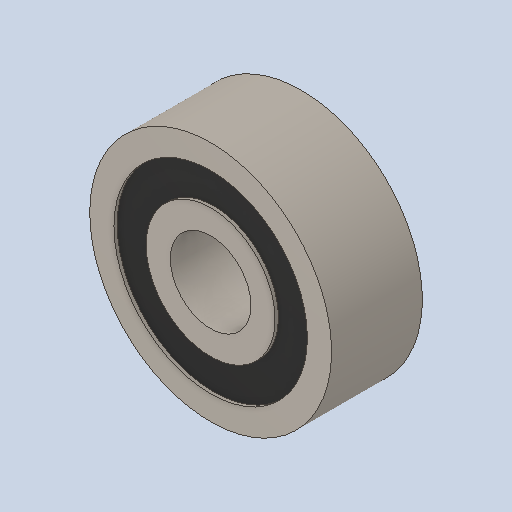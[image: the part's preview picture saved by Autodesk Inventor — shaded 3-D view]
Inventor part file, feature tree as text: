
AUTODESK INVENTOR PART (.ipt)
format: ipt  version: 2023.4 (Build 274418000, 418)  size: 124,416 bytes
history: native  units: in
note: dims shown in document units (in); Inventor stores cm internally (conversion verified against a paired STEP export)
features: revolve x1
ambient origin geometry x8: Origin, YZ Plane, XZ Plane, XY Plane, X Axis, Y Axis, Z Axis, Center Point
bodies: Solid1 (feature_tree)
feature tree (1):
  revolve  "Revolve1"  [1 undecoded]
note: 1 required parameter value undecoded (feature->parameter linkage not recoverable at this tier; creation-order binding heuristic only, values carry confidence <= 0.55)
